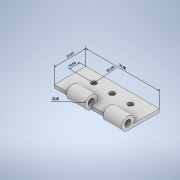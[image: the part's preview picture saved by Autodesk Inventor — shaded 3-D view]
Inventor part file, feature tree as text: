
AUTODESK INVENTOR PART (.ipt)
format: ipt  version: 2021 (Build 250183000, 183)  size: 185,856 bytes
history: native  units: mm
features: other x6, extrude x5, sketch x5
ambient origin geometry x8: Origin, YZ Plane, XZ Plane, XY Plane, X Axis, Y Axis, Z Axis, Center Point
bodies: Solid1 (feature_tree)
feature tree (16):
  other  "Annotations"
  extrude  "Extrusion1"  Depth=70.0mm
  extrude  "Extrusion2"  Depth=17.5mm
  extrude  "Extrusion3"  Depth=17.5mm
  extrude  "Extrusion4"  Depth=5.0mm
  extrude  "Extrusion5"  Depth=3.0mm TaperAngle=0.0deg
  sketch  "Sketch1"  dims[d0=30.0mm d1=70.0mm]
  sketch  "Sketch2"  dims[d2=10.0mm d3=17.5mm]
  sketch  "Sketch3"  dims[d4=17.5mm d5=17.5mm]
  sketch  "Sketch4"  dims[d6=5.0mm d7=5.0mm]
  sketch  "Sketch5"  dims[d8=5.0mm d9=3.0mm d10=0.0mm d11=70.0mm d12=0.0mm d14=6.0mm d15=6.0mm d16=70.0mm d17=0.0mm d18=17.5mm d19=17.5mm d20=17.5mm d21=70.0mm d22=0.0mm d24=17.5mm d25=70.0mm d26=0.0mm d27=16.641389mm d28=6.0mm d29=0.0mm d30=10.0mm d31=30.0mm d32=7.151408mm d33=10.0mm d34=53.636644mm d35=5.0mm d36=0.0mm d37=10.0mm d38=70.0mm d23=0.5mm]
  other  "Radial Dimension 1"
  other  "Linear Dimension 1"
  other  "Linear Dimension 2"
  other  "Diameter Dimension 1"
  other  "Linear Dimension 3"
